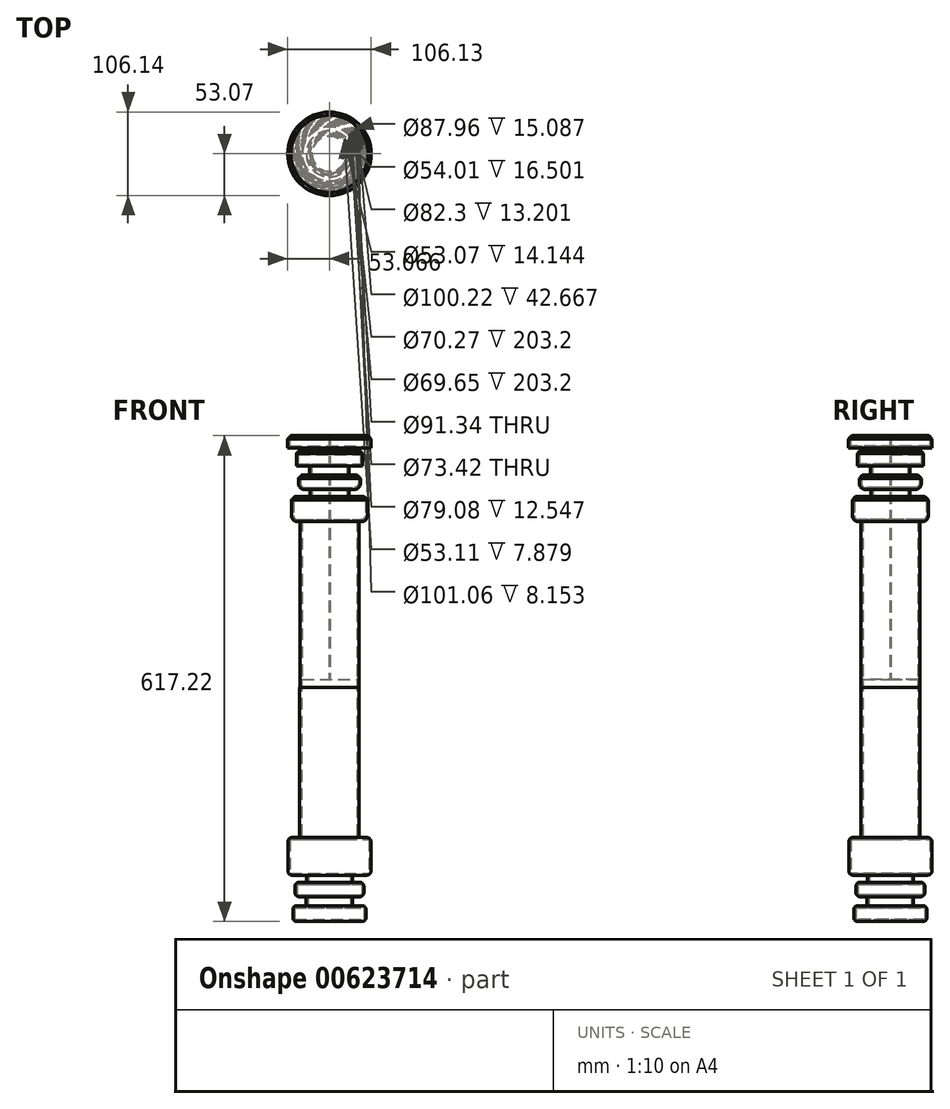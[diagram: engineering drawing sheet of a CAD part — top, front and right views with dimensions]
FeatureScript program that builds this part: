
annotation { "Feature Type Name" : "Feature", "Feature Type Description" : "" }
export const myFeature = defineFeature(function(context is Context, id is Id, definition is map)
    precondition{}
    {
        {
            var Q0;
            Q0=qCreatedBy(makeId("Front.planeOp"),FACE);
            var sketch = newSketch(context, id + "F0", { "sketchPlane" : qUnion([Q0])});
            skLineSegment(sketch, "E0.right", {"start": v(0, 85.57) * mm, "end": v(0, 70.48) * mm});
            skLineSegment(sketch, "E1.left", {"start": v(0, 70.48) * mm, "end": v(0, 53.98) * mm});
            skLineSegment(sketch, "E2.left", {"start": v(0, 53.98) * mm, "end": v(0, 40.78) * mm});
            skLineSegment(sketch, "E3.left", {"start": v(0, 40.78) * mm, "end": v(0, 26.64) * mm});
            skLineSegment(sketch, "E4.left", {"start": v(0, 26.64) * mm, "end": v(0, 0) * mm});
            skLineSegment(sketch, "E5.left", {"start": v(0, 0) * mm, "end": v(0, -203.2) * mm});
            skLineSegment(sketch, "E6.bottom", {"start": v(43.34, -508) * mm, "end": v(-0.64, -508) * mm});
            skLineSegment(sketch, "E6.top", {"start": v(43.34, -492.91) * mm, "end": v(-0.64, -492.91) * mm});
            skLineSegment(sketch, "E6.left", {"start": v(43.34, -508) * mm, "end": v(43.34, -492.91) * mm});
            skLineSegment(sketch, "E6.right", {"start": v(-0.64, -508) * mm, "end": v(-0.64, -492.91) * mm});
            skLineSegment(sketch, "E7.bottom", {"start": v(-0.64, -492.91) * mm, "end": v(26.36, -492.91) * mm});
            skLineSegment(sketch, "E7.top", {"start": v(-0.64, -476.41) * mm, "end": v(26.36, -476.41) * mm});
            skLineSegment(sketch, "E7.left", {"start": v(-0.64, -492.91) * mm, "end": v(-0.64, -476.41) * mm});
            skLineSegment(sketch, "E7.right", {"start": v(26.36, -492.91) * mm, "end": v(26.36, -476.41) * mm});
            skLineSegment(sketch, "E8.bottom", {"start": v(-0.64, -476.41) * mm, "end": v(40.5, -476.41) * mm});
            skLineSegment(sketch, "E8.top", {"start": v(-0.64, -463.21) * mm, "end": v(40.5, -463.21) * mm});
            skLineSegment(sketch, "E8.left", {"start": v(-0.64, -476.41) * mm, "end": v(-0.64, -463.21) * mm});
            skLineSegment(sketch, "E8.right", {"start": v(40.5, -476.41) * mm, "end": v(40.5, -463.21) * mm});
            skLineSegment(sketch, "E9.bottom", {"start": v(-0.64, -463.21) * mm, "end": v(25.9, -463.21) * mm});
            skLineSegment(sketch, "E9.top", {"start": v(-0.64, -449.07) * mm, "end": v(25.9, -449.07) * mm});
            skLineSegment(sketch, "E9.left", {"start": v(-0.64, -463.21) * mm, "end": v(-0.64, -449.07) * mm});
            skLineSegment(sketch, "E9.right", {"start": v(25.9, -463.21) * mm, "end": v(25.9, -449.07) * mm});
            skLineSegment(sketch, "E10.bottom", {"start": v(-0.64, -449.07) * mm, "end": v(49.46, -449.07) * mm});
            skLineSegment(sketch, "E10.top", {"start": v(-0.64, -406.4) * mm, "end": v(49.46, -406.4) * mm});
            skLineSegment(sketch, "E10.left", {"start": v(-0.64, -449.07) * mm, "end": v(-0.64, -406.4) * mm});
            skLineSegment(sketch, "E10.right", {"start": v(49.46, -449.07) * mm, "end": v(49.46, -406.4) * mm});
            skLineSegment(sketch, "E11.bottom", {"start": v(-0.64, -406.4) * mm, "end": v(34.5, -406.4) * mm});
            skLineSegment(sketch, "E11.top", {"start": v(-0.64, -203.2) * mm, "end": v(34.5, -203.2) * mm});
            skLineSegment(sketch, "E11.left", {"start": v(-0.64, -406.4) * mm, "end": v(-0.64, -203.2) * mm});
            skLineSegment(sketch, "E11.right", {"start": v(34.5, -406.4) * mm, "end": v(34.5, -203.2) * mm});
            skLineSegment(sketch, "E12.MirrorCS", {"start": v(36.07, 53.98) * mm, "end": v(36.07, 40.78) * mm});
            skLineSegment(sketch, "E13.MirrorCS", {"start": v(38.9, 85.57) * mm, "end": v(38.9, 70.48) * mm});
            skLineSegment(sketch, "E14.MirrorCS", {"start": v(21.45, 40.78) * mm, "end": v(21.45, 26.64) * mm});
            skLineSegment(sketch, "E15.MirrorCS", {"start": v(0, 26.64) * mm, "end": v(21.45, 26.64) * mm});
            skLineSegment(sketch, "E16.MirrorCS", {"start": v(0, 53.98) * mm, "end": v(21.92, 53.98) * mm});
            skLineSegment(sketch, "E17.MirrorCS", {"start": v(0, 0) * mm, "end": v(34.18, 0) * mm});
            skLineSegment(sketch, "E18.MirrorCS", {"start": v(0, -203.2) * mm, "end": v(34.18, -203.2) * mm});
            skLineSegment(sketch, "E19.MirrorCS", {"start": v(0, 0) * mm, "end": v(45.02, 0) * mm});
            skLineSegment(sketch, "E20.MirrorCS", {"start": v(0, 40.78) * mm, "end": v(36.07, 40.78) * mm});
            skLineSegment(sketch, "E21.MirrorCS", {"start": v(0, 40.78) * mm, "end": v(21.45, 40.78) * mm});
            skLineSegment(sketch, "E22.MirrorCS", {"start": v(0, 26.64) * mm, "end": v(45.02, 26.64) * mm});
            skLineSegment(sketch, "E23.MirrorCS", {"start": v(38.9, 85.57) * mm, "end": v(0, 85.57) * mm});
            skLineSegment(sketch, "E24.MirrorCS", {"start": v(0, 53.98) * mm, "end": v(36.07, 53.98) * mm});
            skLineSegment(sketch, "E25.MirrorCS", {"start": v(21.92, 70.48) * mm, "end": v(21.92, 53.98) * mm});
            skLineSegment(sketch, "E26.MirrorCS", {"start": v(45.02, 26.64) * mm, "end": v(45.02, 0) * mm});
            skLineSegment(sketch, "E27.MirrorCS", {"start": v(38.9, 70.48) * mm, "end": v(0, 70.48) * mm});
            skLineSegment(sketch, "E28.MirrorCS", {"start": v(0, 70.48) * mm, "end": v(21.92, 70.48) * mm});
            skLineSegment(sketch, "E29.MirrorCS", {"start": v(34.18, 0) * mm, "end": v(34.18, -203.2) * mm});
            skLineSegment(sketch, "E30.bottom", {"start": v(0, 85.57) * mm, "end": v(25.9, 85.57) * mm});
            skLineSegment(sketch, "E30.top", {"start": v(0, 93.45) * mm, "end": v(25.9, 93.45) * mm});
            skLineSegment(sketch, "E30.left", {"start": v(0, 85.57) * mm, "end": v(0, 93.45) * mm});
            skLineSegment(sketch, "E30.right", {"start": v(25.9, 85.57) * mm, "end": v(25.9, 93.45) * mm});
            skLineSegment(sketch, "E31.bottom", {"start": v(0, 93.45) * mm, "end": v(49.88, 93.45) * mm});
            skLineSegment(sketch, "E31.top", {"start": v(0, 104.14) * mm, "end": v(49.88, 104.14) * mm});
            skLineSegment(sketch, "E31.left", {"start": v(0, 93.45) * mm, "end": v(0, 104.14) * mm});
            skLineSegment(sketch, "E31.right", {"start": v(49.88, 93.45) * mm, "end": v(49.88, 104.14) * mm});
            skSolve(sketch);
        }
        {
            var Q0;
            {var subQ4=sQuery(id+"F0.wireOp",EDGE,"E5.left");var subQ7=sQuery(id+"F0.wireOp",EDGE,"E11.left");var subQ12=sQuery(id+"F0.wireOp",EDGE,"E3.left");var subQ15=sQuery(id+"F0.wireOp",EDGE,"E2.left");var subQ20=makeQuery(id+"F0.imprint","IMPRINT",EDGE,{"derivedFrom":sQuery(id+"F0.wireOp",EDGE,"E9.top")});var subQ31=sQuery(id+"F0.wireOp",EDGE,"E0.right");var subQ35=makeQuery(id+"F0.imprint","IMPRINT",EDGE,{"derivedFrom":sQuery(id+"F0.wireOp",EDGE,"E30.top")});var subQ36=sQuery(id+"F0.wireOp",EDGE,"E1.left");var subQ42=makeQuery(id+"F0.imprint","IMPRINT",EDGE,{"derivedFrom":sQuery(id+"F0.wireOp",EDGE,"E7.top")});Q0=qUnion([makeQuery(id+"F0.imprint","IMPRINT",FACE,{"disambiguationData":[TD([[makeQuery(id+"F0.imprint","IMPRINT",EDGE,{"derivedFrom":sQuery(id+"F0.wireOp",EDGE,"E4.left")}),1.0]])]}),makeQuery(id+"F0.imprint","IMPRINT",FACE,{"disambiguationData":[TD([[makeQuery(id+"F0.imprint","IMPRINT",EDGE,{"derivedFrom":sQuery(id+"F0.wireOp",EDGE,"E6.bottom")}),-1.0]])]}),makeQuery(id+"F0.imprint","IMPRINT",FACE,{"disambiguationData":[TD([[makeQuery(id+"F0.imprint","IMPRINT",EDGE,{"derivedFrom":subQ4}),1.0]])]}),makeQuery(id+"F0.imprint","IMPRINT",FACE,{"disambiguationData":[TD([[subQ35,1.0]])]}),makeQuery(id+"F0.imprint","IMPRINT",FACE,{"disambiguationData":[TD([[subQ42,-1.0]])]}),makeQuery(id+"F0.imprint","IMPRINT",FACE,{"disambiguationData":[TD([[makeQuery(id+"F0.imprint","IMPRINT",EDGE,{"derivedFrom":subQ31}),1.0]])]}),makeQuery(id+"F0.imprint","IMPRINT",FACE,{"disambiguationData":[TD([[subQ42,1.0]])]}),makeQuery(id+"F0.imprint","IMPRINT",FACE,{"disambiguationData":[TD([[makeQuery(id+"F0.imprint","IMPRINT",EDGE,{"derivedFrom":subQ36}),1.0]])]}),makeQuery(id+"F0.imprint","IMPRINT",FACE,{"disambiguationData":[TD([[subQ35,-1.0]])]}),makeQuery(id+"F0.imprint","IMPRINT",FACE,{"disambiguationData":[TD([[subQ20,-1.0]])]}),makeQuery(id+"F0.imprint","IMPRINT",FACE,{"disambiguationData":[TD([[makeQuery(id+"F0.imprint","IMPRINT",EDGE,{"derivedFrom":subQ15}),1.0]])]}),makeQuery(id+"F0.imprint","IMPRINT",FACE,{"disambiguationData":[TD([[subQ20,1.0]])]}),makeQuery(id+"F0.imprint","IMPRINT",FACE,{"disambiguationData":[TD([[makeQuery(id+"F0.imprint","IMPRINT",EDGE,{"derivedFrom":subQ12}),1.0]])]}),makeQuery(id+"F0.imprint","IMPRINT",FACE,{"disambiguationData":[TD([[makeQuery(id+"F0.imprint","IMPRINT",EDGE,{"derivedFrom":subQ7}),-1.0]])]})]);}
            var Q1;
            Q1=sQuery(id+"F0.wireOp",EDGE,"E11.left");
            revolve(context, id + "F1", {"entities" : qUnion([Q0]), "axis" : qUnion([Q1]), "revolveType" : RevolveType.FULL, "surfaceOperationType" : NewSurfaceOperationType.NEW});
        }
        {
            var Q0;
            Q0=makeQuery(id+"F1.opRevolve","SWEPT_EDGE",EDGE,{"disambiguationData":[OSD([sQuery(id+"F0.wireOp",EDGE,"E31.top"),sQuery(id+"F0.wireOp",EDGE,"E31.right")])]});
            var Q1;
            Q1=makeQuery(id+"F1.opRevolve","SWEPT_EDGE",EDGE,{"disambiguationData":[OSD([sQuery(id+"F0.wireOp",EDGE,"E13.MirrorCS"),sQuery(id+"F0.wireOp",EDGE,"E23.MirrorCS")])]});
            var Q2;
            Q2=makeQuery(id+"F1.opRevolve","SWEPT_EDGE",EDGE,{"disambiguationData":[OSD([sQuery(id+"F0.wireOp",EDGE,"E12.MirrorCS"),sQuery(id+"F0.wireOp",EDGE,"E24.MirrorCS")])]});
            var Q3;
            Q3=makeQuery(id+"F1.opRevolve","SWEPT_EDGE",EDGE,{"disambiguationData":[OSD([sQuery(id+"F0.wireOp",EDGE,"E22.MirrorCS"),sQuery(id+"F0.wireOp",EDGE,"E26.MirrorCS")])]});
            chamfer(context, id + "F2", {"entities" : qUnion([Q0, Q1, Q2, Q3]), "width" : 2.54 * mm, "tangentPropagation" : true});
        }
        {
            var Q0;
            Q0=makeQuery(id+"F1.opRevolve","SWEPT_EDGE",EDGE,{"disambiguationData":[OSD([sQuery(id+"F0.wireOp",EDGE,"E19.MirrorCS"),sQuery(id+"F0.wireOp",EDGE,"E26.MirrorCS")])]});
            var Q1;
            Q1=makeQuery(id+"F1.opRevolve","SWEPT_EDGE",EDGE,{"disambiguationData":[OSD([sQuery(id+"F0.wireOp",EDGE,"E12.MirrorCS"),sQuery(id+"F0.wireOp",EDGE,"E20.MirrorCS")])]});
            var Q2;
            Q2=makeQuery(id+"F1.opRevolve","SWEPT_EDGE",EDGE,{"disambiguationData":[OSD([sQuery(id+"F0.wireOp",EDGE,"E14.MirrorCS"),sQuery(id+"F0.wireOp",EDGE,"E15.MirrorCS"),sQuery(id+"F0.wireOp",EDGE,"E22.MirrorCS")])]});
            fillet(context, id + "F3", {"entities" : qUnion([Q0, Q1, Q2]), "radius" : 5.08 * mm, "tangentPropagation" : true, "allowEdgeOverflow" : false});
        }
        {
            var Q0;
            Q0=makeQuery(id+"F1.opRevolve","SWEPT_FACE",FACE,{"disambiguationData":[OSD([sQuery(id+"F0.wireOp",EDGE,"E31.top")])]});
            var Q1;
            Q1=makeQuery(id+"F1.opRevolve","SWEPT_BODY",BODY,{"disambiguationData":[OSD([sQuery(id+"F0.wireOp",EDGE,"E0.right"),sQuery(id+"F0.wireOp",EDGE,"E1.left"),sQuery(id+"F0.wireOp",EDGE,"E2.left"),sQuery(id+"F0.wireOp",EDGE,"E3.left"),sQuery(id+"F0.wireOp",EDGE,"E4.left"),sQuery(id+"F0.wireOp",EDGE,"E5.left"),sQuery(id+"F0.wireOp",EDGE,"E6.bottom"),sQuery(id+"F0.wireOp",EDGE,"E6.top"),sQuery(id+"F0.wireOp",EDGE,"E6.left"),sQuery(id+"F0.wireOp",EDGE,"E6.right"),sQuery(id+"F0.wireOp",EDGE,"E7.left"),sQuery(id+"F0.wireOp",EDGE,"E7.right"),sQuery(id+"F0.wireOp",EDGE,"E8.bottom"),sQuery(id+"F0.wireOp",EDGE,"E8.top"),sQuery(id+"F0.wireOp",EDGE,"E8.left"),sQuery(id+"F0.wireOp",EDGE,"E8.right"),sQuery(id+"F0.wireOp",EDGE,"E9.left"),sQuery(id+"F0.wireOp",EDGE,"E9.right"),sQuery(id+"F0.wireOp",EDGE,"E10.bottom"),sQuery(id+"F0.wireOp",EDGE,"E10.top"),sQuery(id+"F0.wireOp",EDGE,"E10.left"),sQuery(id+"F0.wireOp",EDGE,"E10.right"),sQuery(id+"F0.wireOp",EDGE,"E11.top"),sQuery(id+"F0.wireOp",EDGE,"E11.left"),sQuery(id+"F0.wireOp",EDGE,"E11.right"),sQuery(id+"F0.wireOp",EDGE,"E12.MirrorCS"),sQuery(id+"F0.wireOp",EDGE,"E13.MirrorCS"),sQuery(id+"F0.wireOp",EDGE,"E14.MirrorCS"),sQuery(id+"F0.wireOp",EDGE,"E19.MirrorCS"),sQuery(id+"F0.wireOp",EDGE,"E20.MirrorCS"),sQuery(id+"F0.wireOp",EDGE,"E22.MirrorCS"),sQuery(id+"F0.wireOp",EDGE,"E23.MirrorCS"),sQuery(id+"F0.wireOp",EDGE,"E24.MirrorCS"),sQuery(id+"F0.wireOp",EDGE,"E25.MirrorCS"),sQuery(id+"F0.wireOp",EDGE,"E26.MirrorCS"),sQuery(id+"F0.wireOp",EDGE,"E27.MirrorCS"),sQuery(id+"F0.wireOp",EDGE,"E29.MirrorCS"),sQuery(id+"F0.wireOp",EDGE,"E30.left"),sQuery(id+"F0.wireOp",EDGE,"E30.right"),sQuery(id+"F0.wireOp",EDGE,"E31.bottom"),sQuery(id+"F0.wireOp",EDGE,"E31.top"),sQuery(id+"F0.wireOp",EDGE,"E31.left"),sQuery(id+"F0.wireOp",EDGE,"E31.right")])]});
            shell(context, id + "F4", {"isHollow" : true, "entities" : qUnion([Q0]), "parts" : qUnion([Q1]), "thickness" : 2.54 * mm, "oppositeDirection" : true});
        }
        {
            var Q0;
            Q0=makeQuery(id+"F1.opRevolve","SWEPT_EDGE",EDGE,{"disambiguationData":[OSD([sQuery(id+"F0.wireOp",EDGE,"E6.bottom"),sQuery(id+"F0.wireOp",EDGE,"E6.left")])]});
            var Q1;
            Q1=makeQuery(id+"F1.opRevolve","SWEPT_EDGE",EDGE,{"disambiguationData":[OSD([sQuery(id+"F0.wireOp",EDGE,"E6.top"),sQuery(id+"F0.wireOp",EDGE,"E6.left")])]});
            var Q2;
            Q2=makeQuery(id+"F1.opRevolve","SWEPT_EDGE",EDGE,{"disambiguationData":[OSD([sQuery(id+"F0.wireOp",EDGE,"E8.bottom"),sQuery(id+"F0.wireOp",EDGE,"E8.right")])]});
            var Q3;
            Q3=makeQuery(id+"F1.opRevolve","SWEPT_EDGE",EDGE,{"disambiguationData":[OSD([sQuery(id+"F0.wireOp",EDGE,"E8.top"),sQuery(id+"F0.wireOp",EDGE,"E8.right")])]});
            var Q4;
            Q4=makeQuery(id+"F1.opRevolve","SWEPT_EDGE",EDGE,{"disambiguationData":[OSD([sQuery(id+"F0.wireOp",EDGE,"E10.bottom"),sQuery(id+"F0.wireOp",EDGE,"E10.right")])]});
            var Q5;
            Q5=makeQuery(id+"F1.opRevolve","SWEPT_EDGE",EDGE,{"disambiguationData":[OSD([sQuery(id+"F0.wireOp",EDGE,"E10.top"),sQuery(id+"F0.wireOp",EDGE,"E10.right")])]});
            fillet(context, id + "F5", {"entities" : qUnion([Q0, Q1, Q2, Q3, Q4, Q5]), "radius" : 5.08 * mm, "tangentPropagation" : true, "allowEdgeOverflow" : false});
        }
        {
            var Q0;
            Q0=makeQuery(id+"F1.opRevolve","SWEPT_EDGE",EDGE,{"disambiguationData":[OSD([sQuery(id+"F0.wireOp",EDGE,"E11.top"),sQuery(id+"F0.wireOp",EDGE,"E11.right")])]});
            chamfer(context, id + "F6", {"entities" : qUnion([Q0]), "width" : 12.7 * mm, "tangentPropagation" : true});
        }
    });
